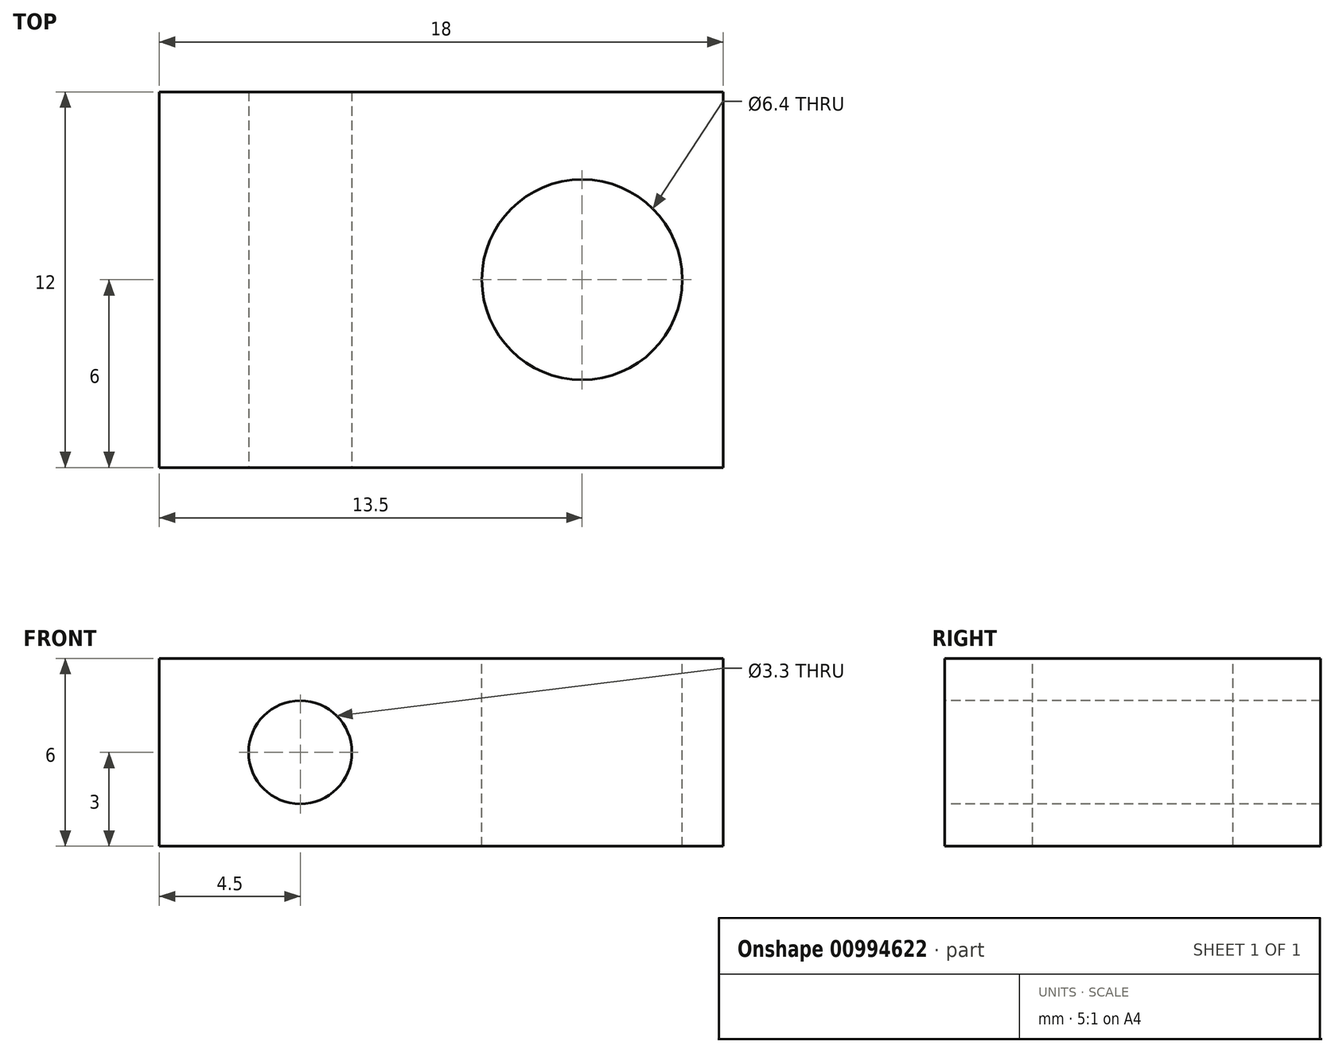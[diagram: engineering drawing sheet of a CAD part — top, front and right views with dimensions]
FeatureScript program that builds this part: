
annotation { "Feature Type Name" : "Feature", "Feature Type Description" : "" }
export const myFeature = defineFeature(function(context is Context, id is Id, definition is map)
    precondition{}
    {
        {
            var Q0;
            Q0=qCreatedBy(makeId("Top.planeOp"),FACE);
            var sketch = newSketch(context, id + "F0", { "sketchPlane" : qUnion([Q0])});
            skLineSegment(sketch, "E0.bottom", {"start": v(-9, 6) * mm, "end": v(9, 6) * mm});
            skLineSegment(sketch, "E0.top", {"start": v(-9, -6) * mm, "end": v(9, -6) * mm});
            skLineSegment(sketch, "E0.left", {"start": v(-9, 6) * mm, "end": v(-9, -6) * mm});
            skLineSegment(sketch, "E0.right", {"start": v(9, 6) * mm, "end": v(9, -6) * mm});
            skPoint(sketch, "E0.middle", {"position": v(0, 0) * mm});
            skSolve(sketch);
        }
        {
            var Q0;
            Q0=makeQuery(id+"F0.imprint","IMPRINT",FACE,{"disambiguationData":[TD([[makeQuery(id+"F0.imprint","IMPRINT",EDGE,{"derivedFrom":sQuery(id+"F0.wireOp",EDGE,"E0.bottom")}),-1.0]])]});
            extrude(context, id + "F1", {"entities" : qUnion([Q0]), "depth" : 6 * mm, "offsetDistance" : 25 * mm});
        }
        {
            var Q0;
            Q0=makeQuery(id+"F1.opExtrude","SWEPT_FACE",FACE,{"disambiguationData":[OSD([sQuery(id+"F0.wireOp",EDGE,"E0.top")])]});
            var sketch = newSketch(context, id + "F2", { "sketchPlane" : qUnion([Q0])});
            skLineSegment(sketch, "E1", {"start": v(0, 6) * mm, "end": v(0, 0) * mm, "construction": true});
            skLineSegment(sketch, "E2", {"start": v(0, 3) * mm, "end": v(-9, 3) * mm, "construction": true});
            skCircle(sketch, "E3", {"center": v(-4.5, 3) * mm, "radius": 1.65 * mm});
            skSolve(sketch);
        }
        {
            var Q0;
            Q0=makeQuery(id+"F1.opExtrude","CAP_FACE",FACE,{"disambiguationData":[OSD([sQuery(id+"F0.wireOp",EDGE,"E0.bottom"),sQuery(id+"F0.wireOp",EDGE,"E0.top"),sQuery(id+"F0.wireOp",EDGE,"E0.left"),sQuery(id+"F0.wireOp",EDGE,"E0.right")])],"isStart":false});
            var sketch = newSketch(context, id + "F3", { "sketchPlane" : qUnion([Q0])});
            skLineSegment(sketch, "E4", {"start": v(0, 0) * mm, "end": v(9, 0) * mm, "construction": true});
            skCircle(sketch, "E5", {"center": v(4.5, 0) * mm, "radius": 3.2 * mm});
            skSolve(sketch);
        }
        {
            var Q0;
            Q0=makeQuery(id+"F2.imprint","IMPRINT",FACE,{"disambiguationData":[TD([[makeQuery(id+"F2.imprint","IMPRINT",EDGE,{"derivedFrom":sQuery(id+"F2.wireOp",EDGE,"E3")}),1.0]])]});
            extrude(context, id + "F4", {"entities" : qUnion([Q0]), "operationType" : NewBodyOperationType.REMOVE, "oppositeDirection" : true, "depth" : 25 * mm, "offsetDistance" : 25 * mm});
        }
        {
            var Q0;
            Q0=makeQuery(id+"F3.imprint","IMPRINT",FACE,{"disambiguationData":[TD([[makeQuery(id+"F3.imprint","IMPRINT",EDGE,{"derivedFrom":sQuery(id+"F3.wireOp",EDGE,"E5")}),1.0]])]});
            extrude(context, id + "F5", {"entities" : qUnion([Q0]), "operationType" : NewBodyOperationType.REMOVE, "oppositeDirection" : true, "depth" : 25 * mm, "offsetDistance" : 25 * mm});
        }
    });
